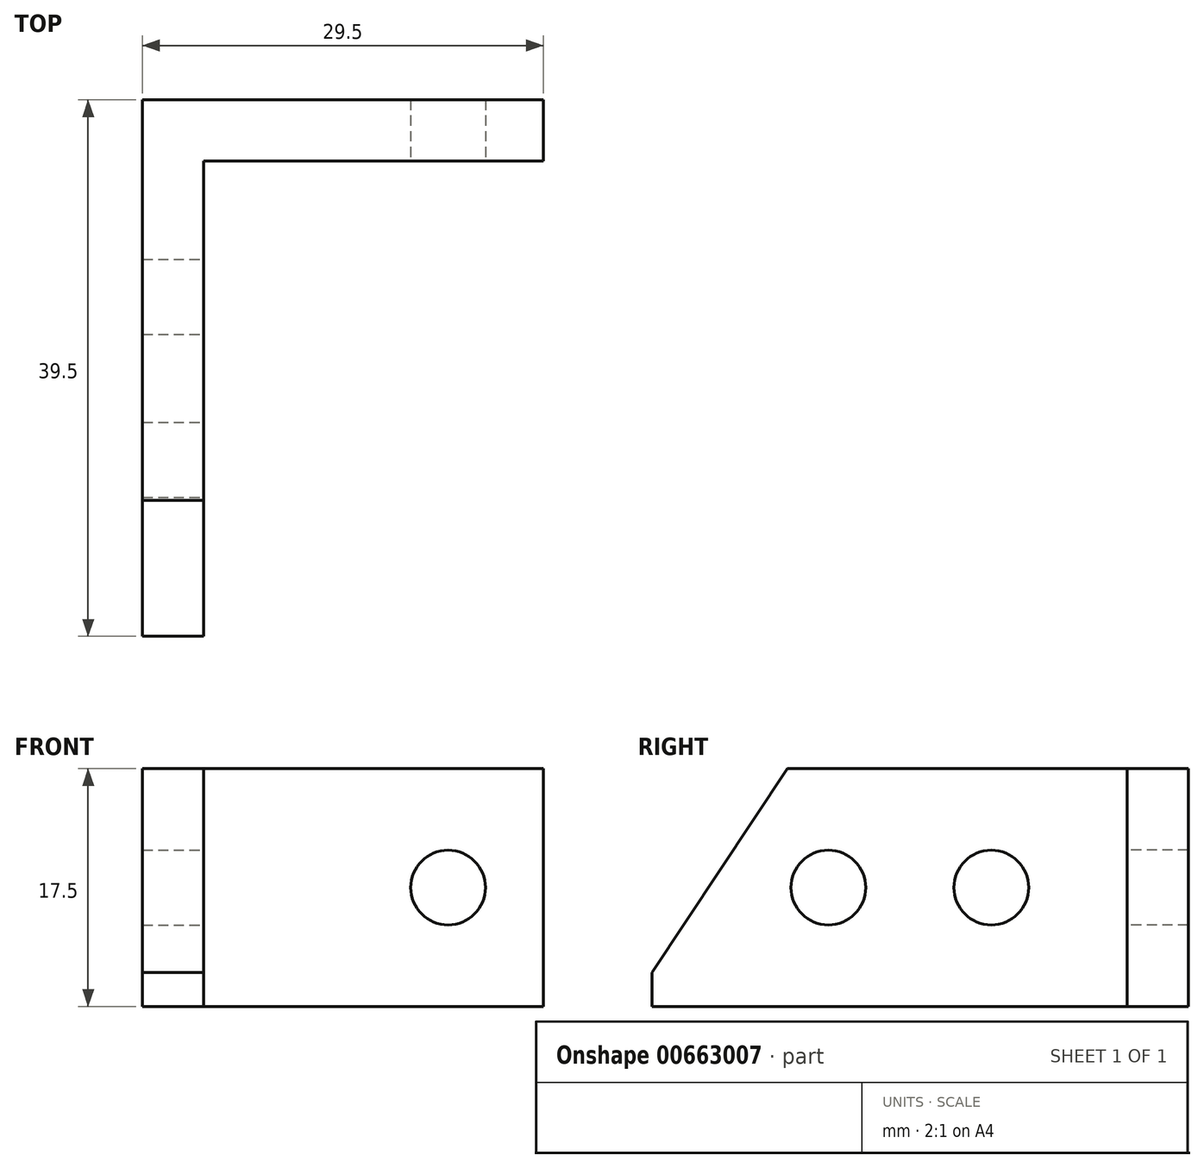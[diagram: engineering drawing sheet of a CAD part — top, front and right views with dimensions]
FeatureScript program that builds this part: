
annotation { "Feature Type Name" : "Feature", "Feature Type Description" : "" }
export const myFeature = defineFeature(function(context is Context, id is Id, definition is map)
    precondition{}
    {
        {
            var Q0;
            Q0=qCreatedBy(makeId("Top.planeOp"),FACE);
            var sketch = newSketch(context, id + "F0", { "sketchPlane" : qUnion([Q0])});
            skLineSegment(sketch, "E0", {"start": v(0, 0) * mm, "end": v(29.5, 0) * mm});
            skLineSegment(sketch, "E1", {"start": v(29.5, 0) * mm, "end": v(29.5, -4.5) * mm});
            skLineSegment(sketch, "E2", {"start": v(29.5, -4.5) * mm, "end": v(4.5, -4.5) * mm});
            skLineSegment(sketch, "E3", {"start": v(4.5, -4.5) * mm, "end": v(4.5, -39.5) * mm});
            skLineSegment(sketch, "E4", {"start": v(4.5, -39.5) * mm, "end": v(0, -39.5) * mm});
            skLineSegment(sketch, "E5", {"start": v(0, -39.5) * mm, "end": v(0, 0) * mm});
            skSolve(sketch);
        }
        {
            var Q0;
            Q0=makeQuery(id+"F0.imprint","IMPRINT",FACE,{"disambiguationData":[TD([[makeQuery(id+"F0.imprint","IMPRINT",EDGE,{"derivedFrom":sQuery(id+"F0.wireOp",EDGE,"E0")}),-1.0]])]});
            extrude(context, id + "F1", {"entities" : qUnion([Q0]), "depth" : 17.5 * mm, "offsetDistance" : 25 * mm});
        }
        {
            var Q0;
            Q0=makeQuery(id+"F1.opExtrude","SWEPT_FACE",FACE,{"disambiguationData":[OSD([sQuery(id+"F0.wireOp",EDGE,"E2")])]});
            var sketch = newSketch(context, id + "F2", { "sketchPlane" : qUnion([Q0])});
            skPoint(sketch, "E6.positionSnap0", {"position": v(29.5, 8.75) * mm});
            skPoint(sketch, "E6.positionSnap1", {"position": v(17, 17.5) * mm});
            skPoint(sketch, "E7", {"position": v(22.5, 8.75) * mm});
            skSolve(sketch);
        }
        {
            var Q0;
            Q0=sQuery(id+"F2.wireOp",VERTEX,"E7");
            var Q1;
            Q1=makeQuery(id+"F1.opExtrude","SWEPT_BODY",BODY,{"disambiguationData":[OSD([sQuery(id+"F0.wireOp",EDGE,"E0"),sQuery(id+"F0.wireOp",EDGE,"E1"),sQuery(id+"F0.wireOp",EDGE,"E2"),sQuery(id+"F0.wireOp",EDGE,"E3"),sQuery(id+"F0.wireOp",EDGE,"E4"),sQuery(id+"F0.wireOp",EDGE,"E5")])]});
            hole(context, id + "F3", {"style" : HoleStyle.SIMPLE, "endStyle" : HoleEndStyle.THROUGH, "standardTappedOrClearance" : lookupTablePath({ "fit" : "Normal", "standard" : "ISO", "size" : "M5", "type" : "Clearance" }), "standardBlindInLast" : lookupTablePath({ "fit" : "Normal", "standard" : "ISO", "engagement" : "75%", "pitch" : "0.8 mm", "size" : "M5", "type" : "Clearance & tapped" }), "holeDiameter" : 5.5 * mm, "majorDiameter" : 5 * mm, "isTappedThrough" : true, "tappedDepth" : 12 * mm, "tapClearance" : 3, "locations" : qUnion([Q0]), "scope" : qUnion([Q1])});
        }
        {
            var Q0;
            Q0=makeQuery(id+"F1.opExtrude","CAP_EDGE",EDGE,{"disambiguationData":[OSD([sQuery(id+"F0.wireOp",EDGE,"E4")])],"isStart":false});
            chamfer(context, id + "F4", {"entities" : qUnion([Q0]), "chamferType" : ChamferType.TWO_OFFSETS, "width1" : 15 * mm, "oppositeDirection" : false, "width2" : 10 * mm, "tangentPropagation" : true});
        }
        {
            var Q0;
            Q0=makeQuery(id+"F1.opExtrude","SWEPT_FACE",FACE,{"disambiguationData":[OSD([sQuery(id+"F0.wireOp",EDGE,"E3")])]});
            var sketch = newSketch(context, id + "F5", { "sketchPlane" : qUnion([Q0])});
            skPoint(sketch, "E8.positionSnap0", {"position": v(-4.5, 8.75) * mm});
            skPoint(sketch, "E9", {"position": v(-14.5, 8.75) * mm});
            skPoint(sketch, "E10", {"position": v(-26.5, 8.75) * mm});
            skSolve(sketch);
        }
        {
            var Q0;
            Q0=sQuery(id+"F5.wireOp",VERTEX,"E9");
            var Q1;
            Q1=sQuery(id+"F5.wireOp",VERTEX,"E10");
            var Q2;
            Q2=makeQuery(id+"F1.opExtrude","SWEPT_BODY",BODY,{"disambiguationData":[OSD([sQuery(id+"F0.wireOp",EDGE,"E0"),sQuery(id+"F0.wireOp",EDGE,"E1"),sQuery(id+"F0.wireOp",EDGE,"E2"),sQuery(id+"F0.wireOp",EDGE,"E3"),sQuery(id+"F0.wireOp",EDGE,"E4"),sQuery(id+"F0.wireOp",EDGE,"E5")])]});
            hole(context, id + "F6", {"style" : HoleStyle.SIMPLE, "endStyle" : HoleEndStyle.THROUGH, "standardTappedOrClearance" : lookupTablePath({ "fit" : "Normal", "standard" : "ISO", "size" : "M5", "type" : "Clearance" }), "standardBlindInLast" : lookupTablePath({ "fit" : "Normal", "standard" : "ISO", "engagement" : "75%", "pitch" : "0.8 mm", "size" : "M5", "type" : "Clearance & tapped" }), "holeDiameter" : 5.5 * mm, "majorDiameter" : 5 * mm, "isTappedThrough" : true, "tappedDepth" : 12 * mm, "tapClearance" : 3, "locations" : qUnion([Q0, Q1]), "scope" : qUnion([Q2])});
        }
    });
